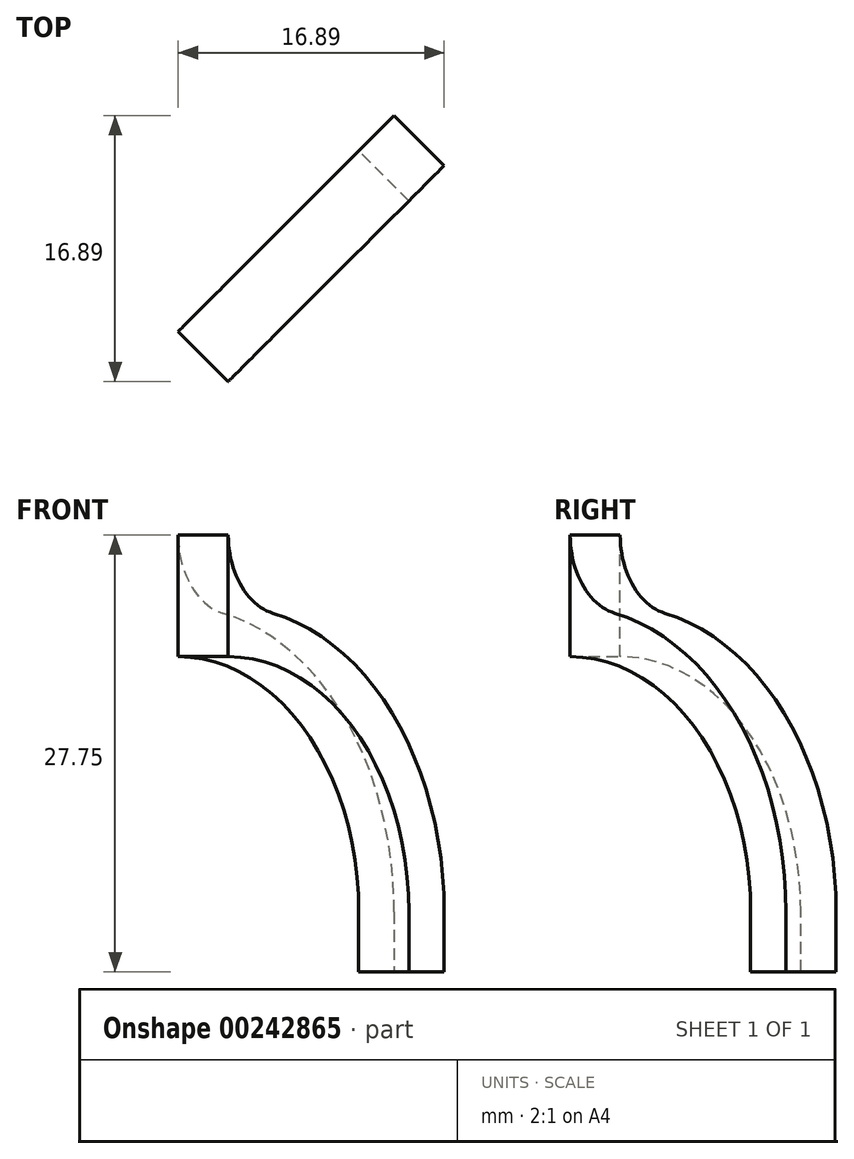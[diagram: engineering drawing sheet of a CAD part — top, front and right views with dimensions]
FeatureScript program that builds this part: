
annotation { "Feature Type Name" : "Feature", "Feature Type Description" : "" }
export const myFeature = defineFeature(function(context is Context, id is Id, definition is map)
    precondition{}
    {
        {
            var Q0;
            Q0=qCreatedBy(makeId("Front.planeOp"),FACE);
            var sketch = newSketch(context, id + "F0", { "sketchPlane" : qUnion([Q0])});
            skLineSegment(sketch, "E0", {"start": v(16.22, 0) * mm, "end": v(19.4, 0) * mm});
            skLineSegment(sketch, "E1", {"start": v(16.22, 0) * mm, "end": v(16.22, 3.8) * mm});
            skLineSegment(sketch, "E2", {"start": v(19.4, 3.81) * mm, "end": v(19.4, 0) * mm});
            skArc(sketch, "E3", {"start": v(19.4, 3.81) * mm, "mid": v(15.07, 16.02) * mm, "end": v(4.03, 22.78) * mm});
            skArc(sketch, "E4", {"start": v(16.22, 3.8) * mm, "mid": v(11.47, 15.28) * mm, "end": v(0, 20.03) * mm});
            skLineSegment(sketch, "E5", {"start": v(0, 23.2) * mm, "end": v(0, 20.03) * mm});
            skLineSegment(sketch, "E6", {"start": v(0, 27.75) * mm, "end": v(0, 29.82) * mm});
            skPoint(sketch, "E7.visualSharp", {"position": v(0, 23.2) * mm});
            skArc(sketch, "E7.filletArc", {"start": v(0, 27.75) * mm, "mid": v(1.13, 24.55) * mm, "end": v(4.03, 22.78) * mm});
            skLineSegment(sketch, "E8", {"start": v(0, 23.2) * mm, "end": v(0, 27.75) * mm});
            skSolve(sketch);
        }
        {
            var Q0;
            Q0=makeQuery(id+"F0.imprint","IMPRINT",FACE,{"disambiguationData":[TD([[makeQuery(id+"F0.imprint","IMPRINT",EDGE,{"derivedFrom":sQuery(id+"F0.wireOp",EDGE,"E0")}),1.0]])]});
            extrude(context, id + "F1", {"entities" : qUnion([Q0]), "flatOperationType" : FlatOperationType.REMOVE, "offsetDistance" : 25.4 * mm, "depth" : 4.5 * mm, "domain" : OperationDomain.MODEL});
        }
        {
            var Q0;
            Q0=makeQuery(id+"F1.opExtrude","SWEPT_BODY",BODY,{"disambiguationData":[OSD([sQuery(id+"F0.wireOp",EDGE,"E0"),sQuery(id+"F0.wireOp",EDGE,"E1"),sQuery(id+"F0.wireOp",EDGE,"E2"),sQuery(id+"F0.wireOp",EDGE,"E3"),sQuery(id+"F0.wireOp",EDGE,"E4"),sQuery(id+"F0.wireOp",EDGE,"E5"),sQuery(id+"F0.wireOp",EDGE,"E7.filletArc"),sQuery(id+"F0.wireOp",EDGE,"E8")])]});
            var Q1;
            Q1=makeQuery(id+"F1.opExtrude","CAP_EDGE",EDGE,{"disambiguationData":[OSD([sQuery(id+"F0.wireOp",EDGE,"E5"),sQuery(id+"F0.wireOp",EDGE,"E8")])],"isStart":false});
            transform(context, id + "F2", {"entities" : qUnion([Q0]), "transformType" : TransformType.ROTATION, "transformAxis" : qUnion([Q1]), "angle" : 45 * degree, "makeCopy" : false});
        }
    });
